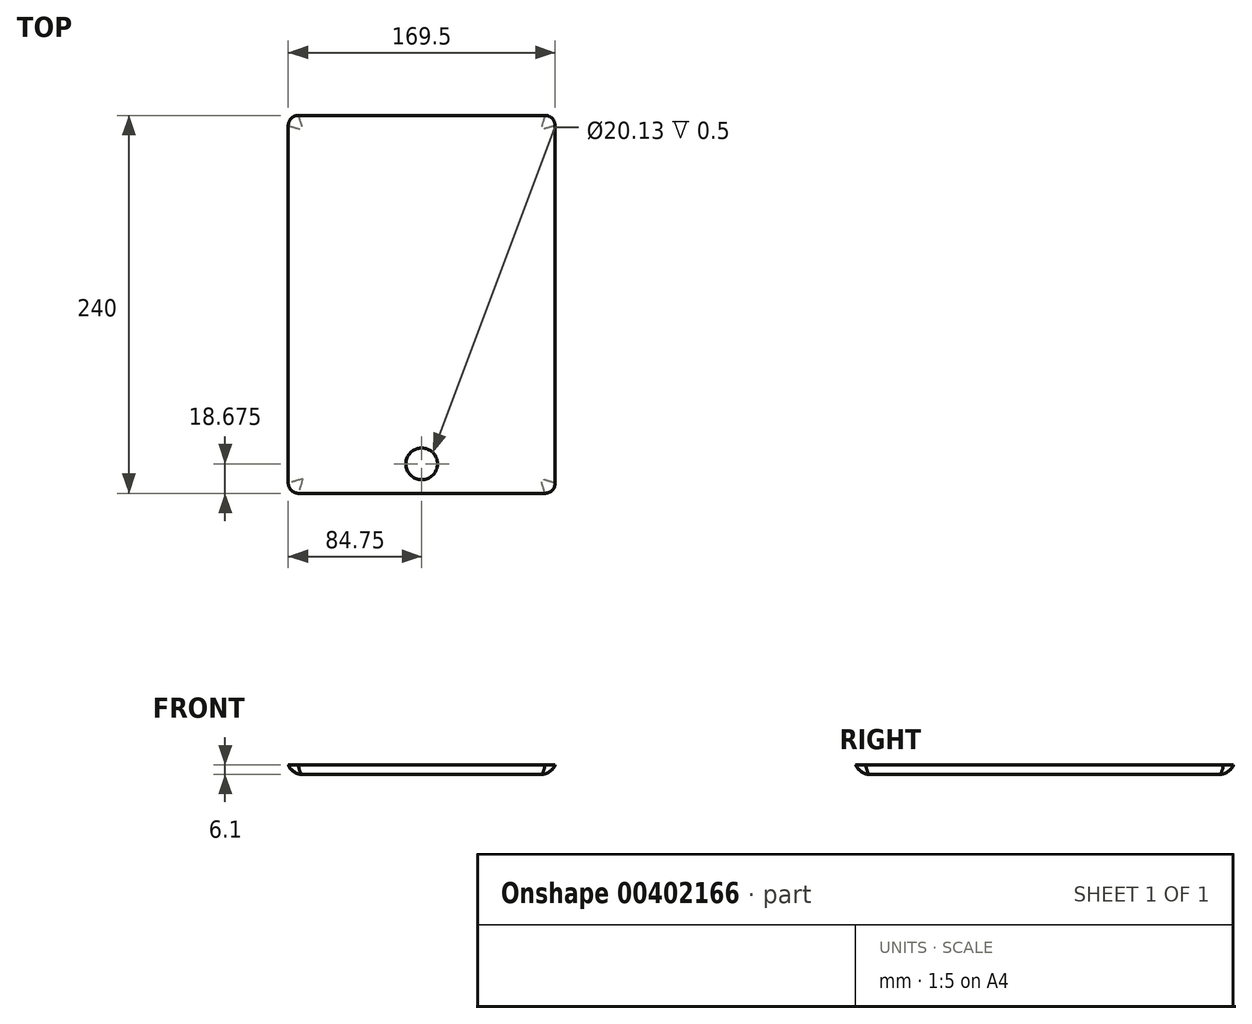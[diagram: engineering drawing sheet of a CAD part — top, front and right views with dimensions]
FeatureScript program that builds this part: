
annotation { "Feature Type Name" : "Feature", "Feature Type Description" : "" }
export const myFeature = defineFeature(function(context is Context, id is Id, definition is map)
    precondition{}
    {
        {
            var Q0;
            Q0=qCreatedBy(makeId("Right.planeOp"),FACE);
            var sketch = newSketch(context, id + "F0", { "sketchPlane" : qUnion([Q0])});
            skLineSegment(sketch, "E0.bottom", {"start": v(-120, 3.05) * mm, "end": v(120, 3.05) * mm});
            skLineSegment(sketch, "E0.top", {"start": v(-120, -3.05) * mm, "end": v(120, -3.05) * mm});
            skLineSegment(sketch, "E0.left", {"start": v(-120, 3.05) * mm, "end": v(-120, -3.05) * mm});
            skLineSegment(sketch, "E0.right", {"start": v(120, 3.05) * mm, "end": v(120, -3.05) * mm});
            skPoint(sketch, "E0.middle", {"position": v(0, 0) * mm});
            skSolve(sketch);
        }
        {
            var Q0;
            Q0 = qSketchRegion(id + "F0", true);
            extrude(context, id + "F1", {"entities" : qUnion([Q0]), "endBound" : BoundingType.SYMMETRIC, "depth" : 169.5 * mm});
        }
        {
            var Q0;
            Q0=makeQuery(id+"F1.opExtrude","SWEPT_EDGE",EDGE,{"disambiguationData":[OSD([sQuery(id+"F0.wireOp",EDGE,"E0.top"),sQuery(id+"F0.wireOp",EDGE,"E0.left")])]});
            var Q1;
            Q1=makeQuery(id+"F1.opExtrude","CAP_EDGE",EDGE,{"disambiguationData":[OSD([sQuery(id+"F0.wireOp",EDGE,"E0.top")])],"isStart":false});
            var Q2;
            Q2=makeQuery(id+"F1.opExtrude","CAP_EDGE",EDGE,{"disambiguationData":[OSD([sQuery(id+"F0.wireOp",EDGE,"E0.top")])],"isStart":true});
            var Q3;
            Q3=makeQuery(id+"F1.opExtrude","SWEPT_EDGE",EDGE,{"disambiguationData":[OSD([sQuery(id+"F0.wireOp",EDGE,"E0.top"),sQuery(id+"F0.wireOp",EDGE,"E0.right")])]});
            fillet(context, id + "F2", {"entities" : qUnion([Q0, Q1, Q2, Q3]), "radius" : 10 * mm, "tangentPropagation" : true, "allowEdgeOverflow" : false});
        }
        {
            var Q0;
            {var subQ0=sQuery(id+"F0.wireOp",EDGE,"E0.top");Q0=makeQuery(id+"F2.opFillet","BLEND_EDGE",EDGE,{"blendedFrom":[makeQuery(id+"F1.opExtrude","SWEPT_EDGE",EDGE,{"disambiguationData":[OSD([subQ0,sQuery(id+"F0.wireOp",EDGE,"E0.right")])]}),makeQuery(id+"F1.opExtrude","CAP_EDGE",EDGE,{"disambiguationData":[OSD([subQ0])],"isStart":false})],"blendedInto":[]});}
            var Q1;
            {var subQ0=sQuery(id+"F0.wireOp",EDGE,"E0.top");Q1=makeQuery(id+"F2.opFillet","BLEND_EDGE",EDGE,{"blendedFrom":[makeQuery(id+"F1.opExtrude","SWEPT_EDGE",EDGE,{"disambiguationData":[OSD([subQ0,sQuery(id+"F0.wireOp",EDGE,"E0.right")])]}),makeQuery(id+"F1.opExtrude","CAP_EDGE",EDGE,{"disambiguationData":[OSD([subQ0])],"isStart":true})],"blendedInto":[]});}
            var Q2;
            {var subQ0=sQuery(id+"F0.wireOp",EDGE,"E0.top");Q2=makeQuery(id+"F2.opFillet","BLEND_EDGE",EDGE,{"blendedFrom":[makeQuery(id+"F1.opExtrude","SWEPT_EDGE",EDGE,{"disambiguationData":[OSD([subQ0,sQuery(id+"F0.wireOp",EDGE,"E0.left")])]}),makeQuery(id+"F1.opExtrude","CAP_EDGE",EDGE,{"disambiguationData":[OSD([subQ0])],"isStart":true})],"blendedInto":[]});}
            var Q3;
            {var subQ0=sQuery(id+"F0.wireOp",EDGE,"E0.top");Q3=makeQuery(id+"F2.opFillet","BLEND_EDGE",EDGE,{"blendedFrom":[makeQuery(id+"F1.opExtrude","SWEPT_EDGE",EDGE,{"disambiguationData":[OSD([subQ0,sQuery(id+"F0.wireOp",EDGE,"E0.left")])]}),makeQuery(id+"F1.opExtrude","CAP_EDGE",EDGE,{"disambiguationData":[OSD([subQ0])],"isStart":false})],"blendedInto":[]});}
            fillet(context, id + "F3", {"entities" : qUnion([Q0, Q1, Q2, Q3]), "radius" : 7 * mm, "tangentPropagation" : true, "allowEdgeOverflow" : false});
        }
        {
            var Q0;
            Q0=makeQuery(id+"F1.opExtrude","SWEPT_FACE",FACE,{"disambiguationData":[OSD([sQuery(id+"F0.wireOp",EDGE,"E0.bottom")])]});
            var sketch = newSketch(context, id + "F4", { "sketchPlane" : qUnion([Q0])});
            skPoint(sketch, "E1.middle", {"position": v(0, 0) * mm});
            skCircle(sketch, "E2", {"center": v(0, -101.33) * mm, "radius": 10.07 * mm});
            skSolve(sketch);
        }
        {
            var Q0;
            Q0 = qSketchRegion(id + "F4", true);
            extrude(context, id + "F5", {"entities" : qUnion([Q0]), "operationType" : NewBodyOperationType.REMOVE, "oppositeDirection" : true, "depth" : 0.5 * mm});
        }
    });
